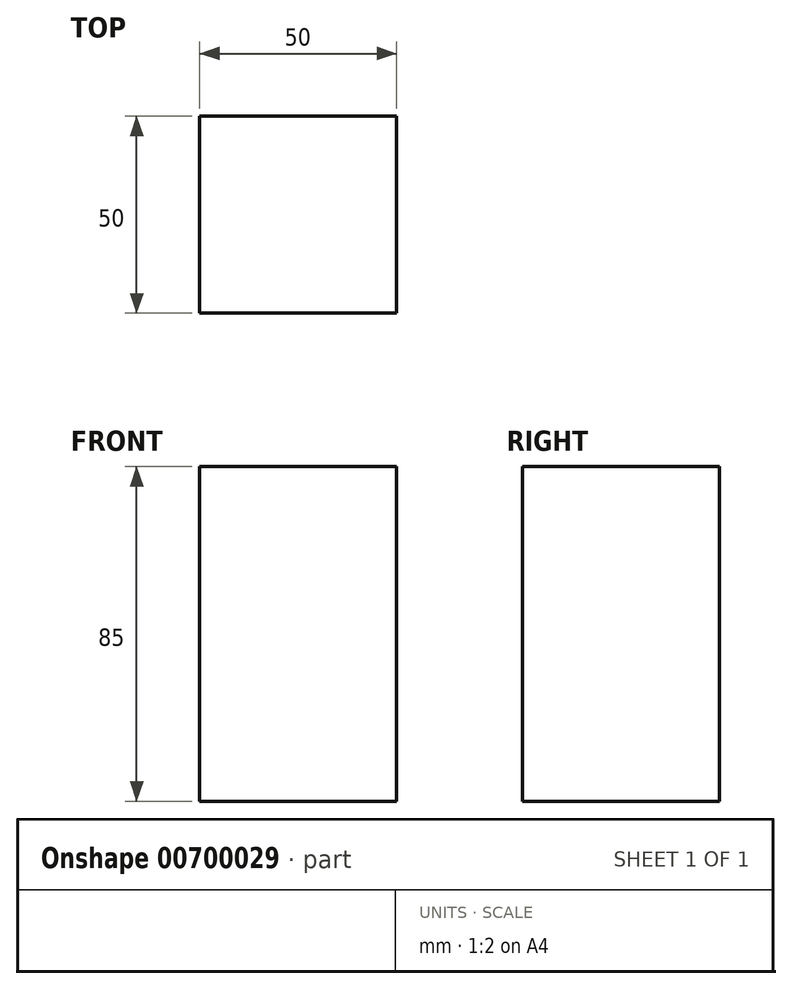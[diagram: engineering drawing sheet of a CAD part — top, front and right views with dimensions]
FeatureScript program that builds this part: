
annotation { "Feature Type Name" : "Feature", "Feature Type Description" : "" }
export const myFeature = defineFeature(function(context is Context, id is Id, definition is map)
    precondition{}
    {
        {
            var Q0;
            Q0=qCreatedBy(makeId("Top.planeOp"),FACE);
            var sketch = newSketch(context, id + "F0", { "sketchPlane" : qUnion([Q0])});
            skLineSegment(sketch, "E0.bottom", {"start": v(25, -25) * mm, "end": v(-25, -25) * mm});
            skLineSegment(sketch, "E0.top", {"start": v(25, 25) * mm, "end": v(-25, 25) * mm});
            skLineSegment(sketch, "E0.left", {"start": v(25, -25) * mm, "end": v(25, 25) * mm});
            skLineSegment(sketch, "E0.right", {"start": v(-25, -25) * mm, "end": v(-25, 25) * mm});
            skPoint(sketch, "E0.middle", {"position": v(0, 0) * mm});
            skSolve(sketch);
        }
        {
            var Q0;
            Q0 = qSketchRegion(id + "F0", true);
            extrude(context, id + "F1", {"entities" : qUnion([Q0]), "depth" : 85 * mm, "offsetDistance" : 25 * mm});
        }
    });
